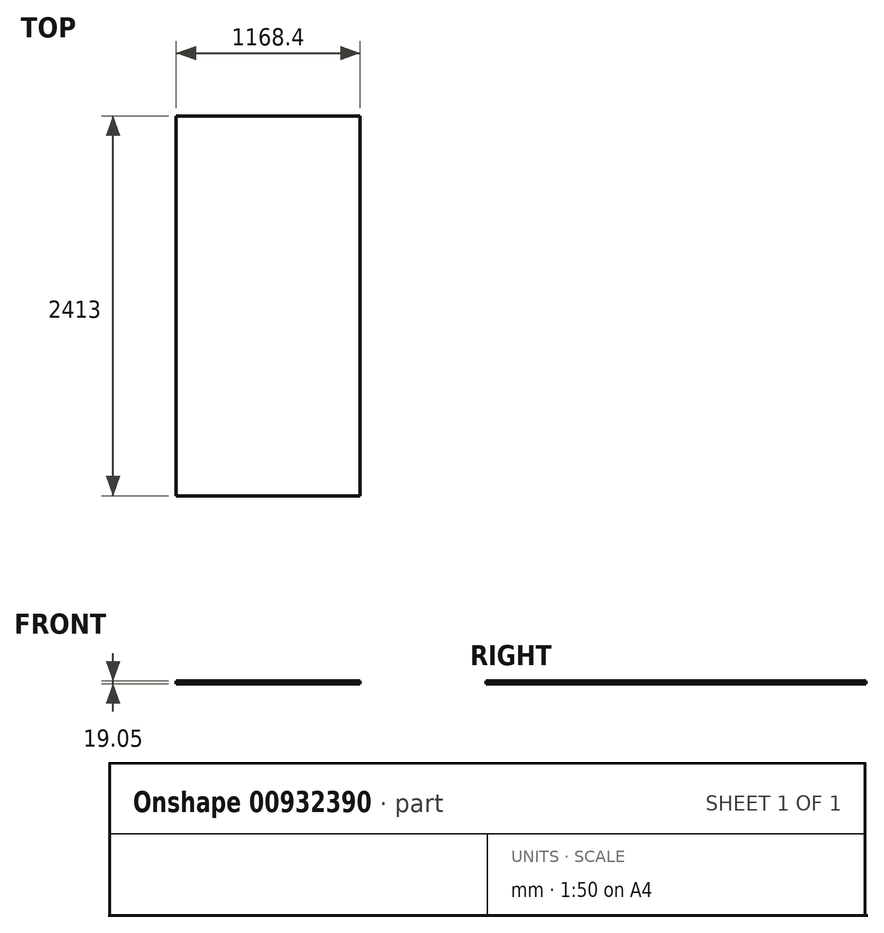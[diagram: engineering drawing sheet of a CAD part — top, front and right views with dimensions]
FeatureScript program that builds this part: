
annotation { "Feature Type Name" : "Feature", "Feature Type Description" : "" }
export const myFeature = defineFeature(function(context is Context, id is Id, definition is map)
    precondition{}
    {
        {
            var Q0;
            Q0=qCreatedBy(makeId("Top.planeOp"),FACE);
            var sketch = newSketch(context, id + "F0", { "sketchPlane" : qUnion([Q0])});
            skLineSegment(sketch, "E0.bottom", {"start": v(584.2, 1206.5) * mm, "end": v(-584.2, 1206.5) * mm});
            skLineSegment(sketch, "E0.top", {"start": v(584.2, -1206.5) * mm, "end": v(-584.2, -1206.5) * mm});
            skLineSegment(sketch, "E0.left", {"start": v(584.2, 1206.5) * mm, "end": v(584.2, -1206.5) * mm});
            skLineSegment(sketch, "E0.right", {"start": v(-584.2, 1206.5) * mm, "end": v(-584.2, -1206.5) * mm});
            skPoint(sketch, "E0.middle", {"position": v(0, 0) * mm});
            skSolve(sketch);
        }
        {
            var Q0;
            Q0=makeQuery(id+"F0.imprint","IMPRINT",FACE,{"disambiguationData":[TD([[makeQuery(id+"F0.imprint","IMPRINT",EDGE,{"derivedFrom":sQuery(id+"F0.wireOp",EDGE,"E0.bottom")}),1.0]])]});
            extrude(context, id + "F1", {"entities" : qUnion([Q0]), "depth" : 19.05 * mm, "offsetDistance" : 25.4 * mm});
        }
    });
